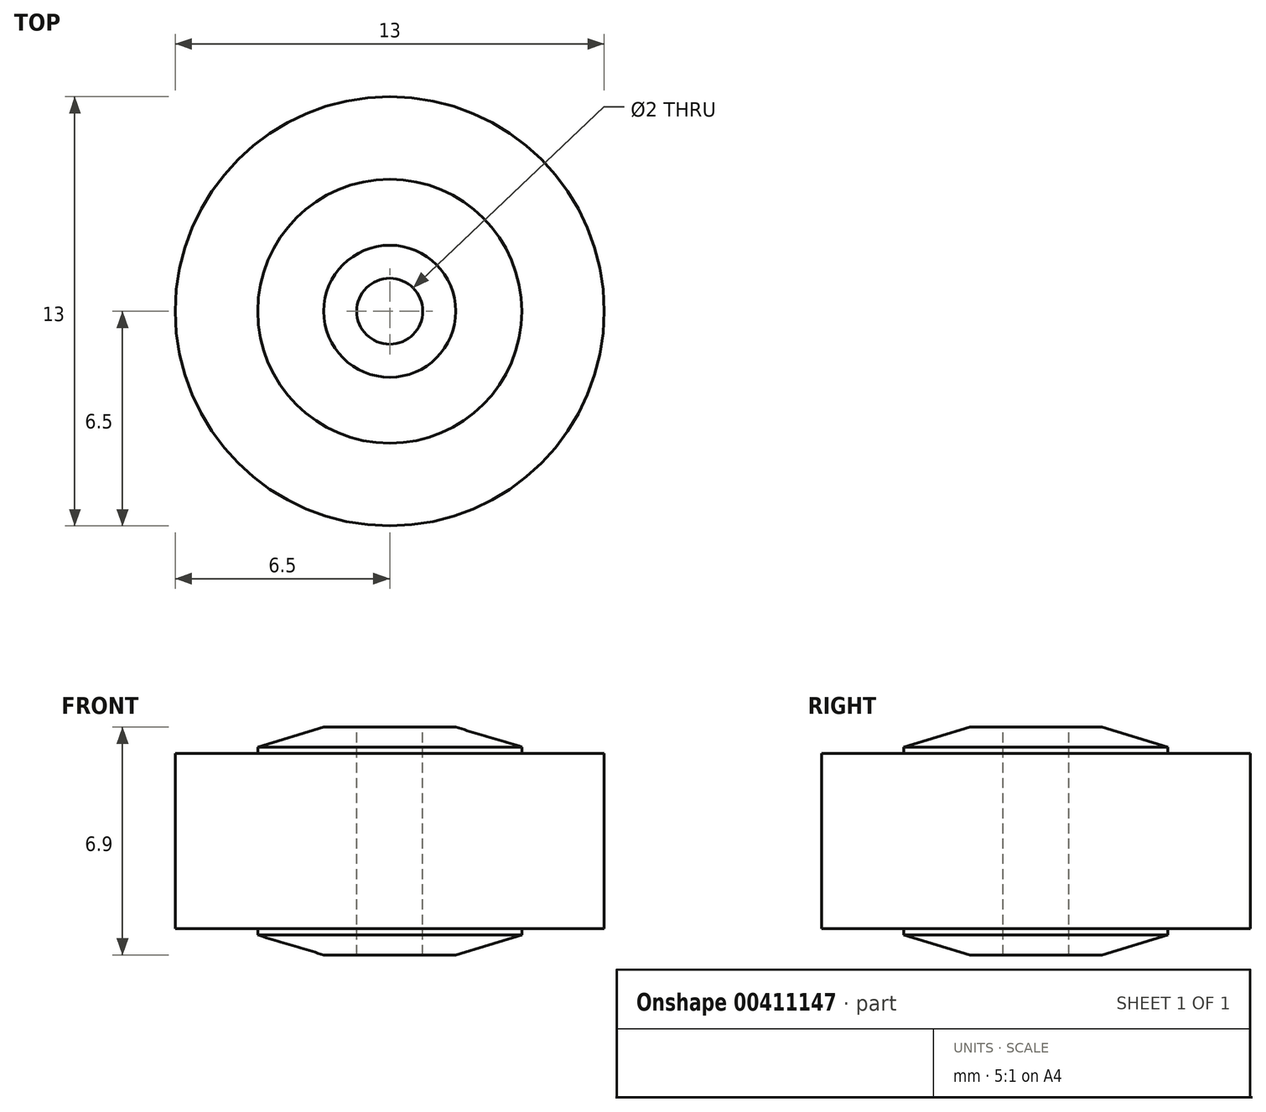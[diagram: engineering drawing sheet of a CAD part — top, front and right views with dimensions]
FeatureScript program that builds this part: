
annotation { "Feature Type Name" : "Feature", "Feature Type Description" : "" }
export const myFeature = defineFeature(function(context is Context, id is Id, definition is map)
    precondition{}
    {
        {
            var Q0;
            Q0=qCreatedBy(makeId("Top.planeOp"),FACE);
            var sketch = newSketch(context, id + "F0", { "sketchPlane" : qUnion([Q0])});
            skCircle(sketch, "E0", {"center": v(0, 0) * mm, "radius": 6.5 * mm});
            skSolve(sketch);
        }
        {
            var Q0;
            Q0 = qSketchRegion(id + "F0", true);
            extrude(context, id + "F1", {"entities" : qUnion([Q0]), "depth" : 5.3 * mm});
        }
        {
            var Q0;
            Q0=makeQuery(id+"F1.opExtrude","CAP_FACE",FACE,{"disambiguationData":[OSD([sQuery(id+"F0.wireOp",EDGE,"E0")])],"isStart":false});
            var sketch = newSketch(context, id + "F2", { "sketchPlane" : qUnion([Q0])});
            skCircle(sketch, "E1", {"center": v(0, 0) * mm, "radius": 4 * mm});
            skSolve(sketch);
        }
        {
            var Q0;
            Q0 = qSketchRegion(id + "F2", true);
            extrude(context, id + "F3", {"entities" : qUnion([Q0]), "operationType" : NewBodyOperationType.ADD, "depth" : 0.8 * mm});
        }
        {
            var Q0;
            Q0=makeQuery(id+"F1.opExtrude","CAP_FACE",FACE,{"disambiguationData":[OSD([sQuery(id+"F0.wireOp",EDGE,"E0")])],"isStart":true});
            var sketch = newSketch(context, id + "F4", { "sketchPlane" : qUnion([Q0])});
            skCircle(sketch, "E2", {"center": v(0, 0) * mm, "radius": 4 * mm});
            skSolve(sketch);
        }
        {
            var Q0;
            Q0 = qSketchRegion(id + "F4", true);
            extrude(context, id + "F5", {"entities" : qUnion([Q0]), "operationType" : NewBodyOperationType.ADD, "depth" : 0.8 * mm});
        }
        {
            var Q0;
            Q0=makeQuery(id+"F5.opExtrude","CAP_EDGE",EDGE,{"disambiguationData":[OSD([sQuery(id+"F4.wireOp",EDGE,"E2")])],"isStart":false});
            var Q1;
            Q1=makeQuery(id+"F3.opExtrude","CAP_EDGE",EDGE,{"disambiguationData":[OSD([sQuery(id+"F2.wireOp",EDGE,"E1")])],"isStart":false});
            chamfer(context, id + "F6", {"entities" : qUnion([Q0, Q1]), "chamferType" : ChamferType.TWO_OFFSETS, "width1" : 2 * mm, "oppositeDirection" : false, "width2" : 0.6 * mm, "tangentPropagation" : true});
        }
        {
            var Q0;
            Q0=makeQuery(id+"F3.opExtrude","CAP_FACE",FACE,{"disambiguationData":[OSD([sQuery(id+"F2.wireOp",EDGE,"E1")])],"isStart":false});
            var sketch = newSketch(context, id + "F7", { "sketchPlane" : qUnion([Q0])});
            skCircle(sketch, "E3", {"center": v(0, 0) * mm, "radius": 1 * mm});
            skSolve(sketch);
        }
        {
            var Q0;
            Q0 = qSketchRegion(id + "F7", true);
            extrude(context, id + "F8", {"entities" : qUnion([Q0]), "operationType" : NewBodyOperationType.REMOVE, "endBound" : BoundingType.UP_TO_NEXT, "oppositeDirection" : true, "depth" : 25 * mm});
        }
    });
